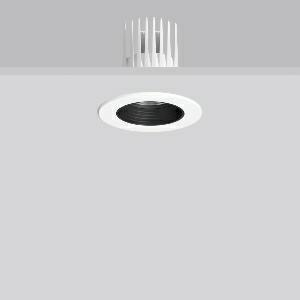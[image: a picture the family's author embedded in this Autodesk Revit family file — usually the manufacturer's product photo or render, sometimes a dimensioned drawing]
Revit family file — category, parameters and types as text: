
# Revit family: heledon_mini_e_901755_002_1_8ed9
name_source: partatom
category: Lighting Fixtures
units: mm (PartAtom-declared; Revit-internal decimal feet)

## family parameters
Cut with Voids When Loaded = No
Host = Face
Light Source = No
Part Type = Normal
Room Calculation Point = No
Round Connector Dimension = Use Diameter
Shared = No

## types (1)
- HELEDON mini E (1 x LED Modul 940, 2950 lm, 4000)
    Apparent Load = 29 VA
    Approval mark = CE
    CIE Flux Codes = 95 100 100 100 100
    Color Rendering = 92
    Color Temperature = 4000
    Default Elevation = 1800 mm
    Description = Series: HELEDON mini
Round recessed downlight. Housing: die-cast aluminium, powder-coated. Black plastic ring and recessed LED to prevent glare from the side. Optical assembly with lens made of plastic (polycarbonate) for the best homogeneous light distribution - can be changed without tools. Best colour rendering index Ra>90. Suitable for Recessed ceiling mounting. Installation without tools thanks to spring fastening system. Including separate LED converter with connecting cable 600 mm.High quality converter without flickering and stroboscopic effect. Through-wiring box (5 pole) available as accessory. The following accessories can be mounted without use of tools: interchangeable lenses, decorative glasses, honeycomb louvre, clear and frosted diffusers, white interchangeable plastic ring. 
Colour: traffic white, matt (RAL 9016)
Diameter: 124 mm
Height: 3 mm
Cut-out diameter: 114 mm
Recess height: 170 mm
Luminaire: recess height: 120 mm
Lamp: LED
Socket: without socket
Colour temperature: 4000K
Colour rendering index (CRI): 92
System power: 29 W
Rated luminous flux: 2950 lm
Luminous efficiency: 102 lm/W
Control gear: Regulated power supply
Protection class: II
Type of protection: IP 20
    Height = 0 mm  [stored 0 ft]
    Lamp = 1 x LED Modul 940
    Lamp Light Flux = 2950 lm
    Lamp count = 1
    Length = 124 mm  [stored 0.406824 ft]
    Lifetime = 50000 h
    Luminous efficacy = 102 lm/W
    Manufacturer = RZB
    ModVariant = No
    Model = 901755.002.1
    Mounting Place = Ceiling
    Mounting Type = Recessed
    Number of Poles = 1
    OnlyDefault = Yes
    Power Factor = 1
    Product Name = HELEDON mini E
    Product group = Recessed downlights
    ProductGroupID = 402
    Protection Class = Protection class II
    Protection Degree = IP 20
    RLX_Detail_Level = 1
    RLX_Emergency_Light_Flux = 0 lm
    RLX_Emergency_Type = 0
    RLX_Emergency_Type_DB = No
    RlxData = <blob elided: 134401 chars, md5=b153615d>
    Socket = socket
    Standby Power = 0 W
    System Light Flux = 2950 lm
    System Power = 29 W
    Type Comments = Product without accessories
    Type Image = 901656.002.jpg
    URL = http://relux.com
    VarID = ---
    Voltage = 230 V
    Voltage Range = 220-240 V
    Weight = 0.00 kg
    Width = 0 mm  [stored 0 ft]

note: [stored X ft] marks values corroborated as IEEE doubles in the binary element streams (Revit-internal decimal feet)

## geometry (parser evidence)
native form markers: Blend x4, Sweep x9
no freeform markers — native parametric forms only
